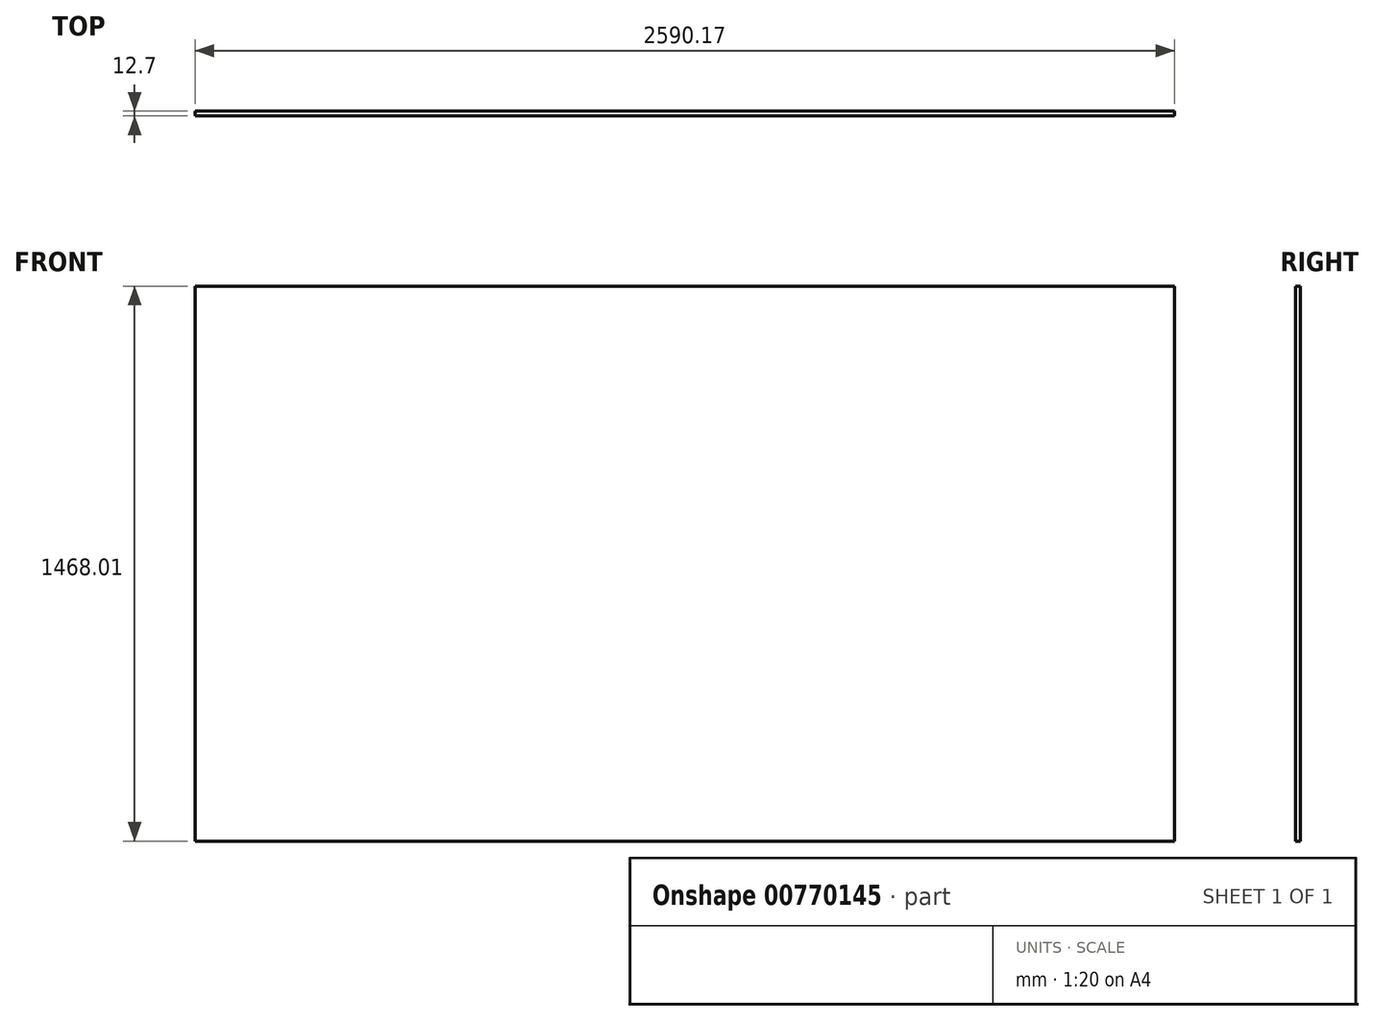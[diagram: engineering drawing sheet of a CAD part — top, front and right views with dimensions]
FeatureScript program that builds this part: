
annotation { "Feature Type Name" : "Feature", "Feature Type Description" : "" }
export const myFeature = defineFeature(function(context is Context, id is Id, definition is map)
    precondition{}
    {
        {
            var Q0;
            Q0=qCreatedBy(makeId("Front.planeOp"),FACE);
            var sketch = newSketch(context, id + "F0", { "sketchPlane" : qUnion([Q0])});
            skLineSegment(sketch, "E0.bottom", {"start": v(-1300.06, 735.25) * mm, "end": v(1290.1, 735.25) * mm});
            skLineSegment(sketch, "E0.top", {"start": v(-1300.06, -732.76) * mm, "end": v(1290.1, -732.76) * mm});
            skLineSegment(sketch, "E0.left", {"start": v(-1300.06, 735.25) * mm, "end": v(-1300.06, -732.76) * mm});
            skLineSegment(sketch, "E0.right", {"start": v(1290.1, 735.25) * mm, "end": v(1290.1, -732.76) * mm});
            skSolve(sketch);
        }
        {
            var Q0;
            Q0=makeQuery(id+"F0.imprint","IMPRINT",FACE,{"disambiguationData":[TD([[makeQuery(id+"F0.imprint","IMPRINT",EDGE,{"derivedFrom":sQuery(id+"F0.wireOp",EDGE,"E0.bottom")}),-1.0]])]});
            extrude(context, id + "F1", {"entities" : qUnion([Q0]), "depth" : 12.7 * mm, "offsetDistance" : 25.4 * mm});
        }
    });
